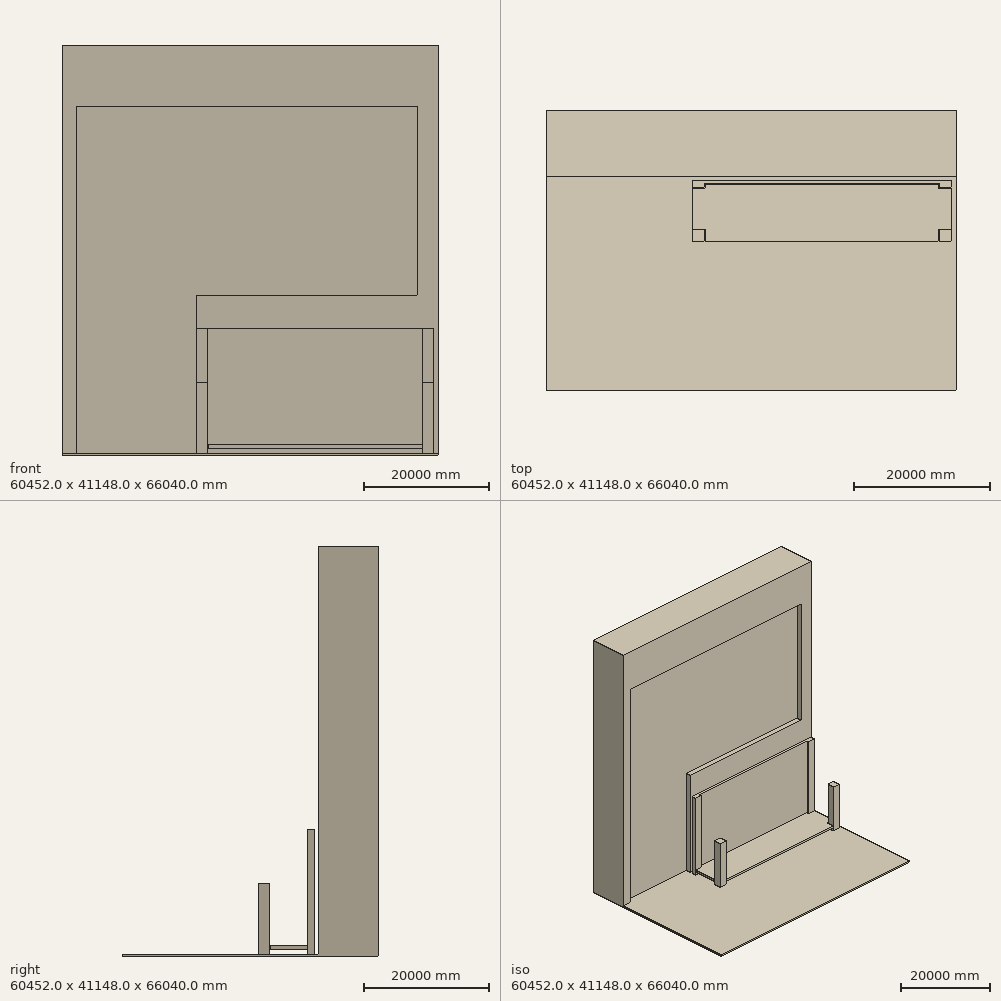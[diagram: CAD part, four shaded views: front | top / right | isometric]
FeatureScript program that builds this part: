
annotation { "Feature Type Name" : "Feature", "Feature Type Description" : "" }
export const myFeature = defineFeature(function(context is Context, id is Id, definition is map)
    precondition{}
    {
        {
            var Q0;
            Q0=qCreatedBy(makeId("Top.planeOp"),FACE);
            var sketch = newSketch(context, id + "F0", { "sketchPlane" : qUnion([Q0])});
            skLineSegment(sketch, "E0.bottom", {"start": v(-60452, 41148) * mm, "end": v(0, 41148) * mm});
            skLineSegment(sketch, "E0.top", {"start": v(-60452, 0) * mm, "end": v(0, 0) * mm});
            skLineSegment(sketch, "E0.left", {"start": v(-60452, 41148) * mm, "end": v(-60452, 0) * mm});
            skLineSegment(sketch, "E0.right", {"start": v(0, 41148) * mm, "end": v(0, 0) * mm});
            skSolve(sketch);
        }
        {
            var Q0;
            Q0=makeQuery(id+"F0.imprint","IMPRINT",FACE,{"disambiguationData":[TD([[makeQuery(id+"F0.imprint","IMPRINT",EDGE,{"derivedFrom":sQuery(id+"F0.wireOp",EDGE,"E0.bottom")}),-1.0]])]});
            extrude(context, id + "F1", {"entities" : qUnion([Q0]), "depth" : 381 * mm, "offsetDistance" : 25.4 * mm});
        }
        {
            var Q0;
            Q0=qCreatedBy(makeId("Top.planeOp"),FACE);
            var sketch = newSketch(context, id + "F2", { "sketchPlane" : qUnion([Q0])});
            skLineSegment(sketch, "E1.bottom", {"start": v(0, 41148) * mm, "end": v(-60452, 41148) * mm});
            skLineSegment(sketch, "E1.top", {"start": v(0, 31496) * mm, "end": v(-60452, 31496) * mm});
            skLineSegment(sketch, "E1.left", {"start": v(0, 41148) * mm, "end": v(0, 31496) * mm});
            skLineSegment(sketch, "E2.right", {"start": v(-60452, 41148) * mm, "end": v(-60452, 31496) * mm});
            skSolve(sketch);
        }
        {
            var Q0;
            Q0 = qSketchRegion(id + "F2", true);
            extrude(context, id + "F3", {"entities" : qUnion([Q0]), "operationType" : NewBodyOperationType.ADD, "depth" : 66040 * mm, "offsetDistance" : 25.4 * mm});
        }
        {
            var Q0;
            Q0=qCreatedBy(makeId("Front.planeOp"),FACE);
            var sketch = newSketch(context, id + "F4", { "sketchPlane" : qUnion([Q0])});
            skLineSegment(sketch, "E3.top", {"start": v(-58293, 381) * mm, "end": v(-38862, 381) * mm});
            skLineSegment(sketch, "E3.left", {"start": v(-58293, 56261) * mm, "end": v(-58293, 381) * mm});
            skLineSegment(sketch, "E3.right", {"start": v(-38862, 25781) * mm, "end": v(-38862, 381) * mm});
            skLineSegment(sketch, "E4.bottom", {"start": v(-38862, 25781) * mm, "end": v(-3302, 25781) * mm});
            skLineSegment(sketch, "E4.right", {"start": v(-3302, 25781) * mm, "end": v(-3302, 56261) * mm});
            skLineSegment(sketch, "E5", {"start": v(-58293, 56261) * mm, "end": v(-3302, 56261) * mm});
            skSolve(sketch);
        }
        {
            var Q0;
            Q0=makeQuery(id+"F4.imprint","IMPRINT",FACE,{"disambiguationData":[TD([[makeQuery(id+"F4.imprint","IMPRINT",EDGE,{"derivedFrom":sQuery(id+"F4.wireOp",EDGE,"E3.top")}),1.0]])]});
            var Q1;
            Q1=sQuery(id+"F0.wireOp",EDGE,"E0.left");
            sweep(context, id + "F5", {"operationType" : NewBodyOperationType.REMOVE, "profiles" : qUnion([Q0]), "path" : qUnion([Q1])});
        }
        {
            var Q0;
            Q0 = qSketchRegion(id + "F4", true);
            extrude(context, id + "F6", {"entities" : qUnion([Q0]), "oppositeDirection" : true, "depth" : 2540 * mm, "offsetDistance" : 25.4 * mm});
        }
        {
            var Q0;
            Q0=makeQuery(id+"F6.opExtrude","SWEPT_BODY",BODY,{"disambiguationData":[OSD([sQuery(id+"F4.wireOp",EDGE,"E3.top"),sQuery(id+"F4.wireOp",EDGE,"E3.left"),sQuery(id+"F4.wireOp",EDGE,"E3.right"),sQuery(id+"F4.wireOp",EDGE,"E4.bottom"),sQuery(id+"F4.wireOp",EDGE,"E4.right"),sQuery(id+"F4.wireOp",EDGE,"E5")])]});
            var Q1;
            Q1=qCreatedBy(makeId("Front.planeOp"),FACE);
            transform(context, id + "F7", {"entities" : qUnion([Q0]), "transformType" : TransformType.TRANSLATION_DISTANCE, "transformDirection" : qUnion([Q1]), "distance" : 32766 * mm, "oppositeDirection" : true, "makeCopy" : false});
        }
        {
            var Q0;
            Q0=qCreatedBy(makeId("Top.planeOp"),FACE);
            cPlane(context, id + "F8", {"entities" : qUnion([Q0]), "cplaneType" : CPlaneType.OFFSET, "offset" : 27432 * mm, "width" : 152.4 * mm, "height" : 152.4 * mm});
        }
        {
            var Q0;
            {var subQ0=sQuery(id+"F0.wireOp",EDGE,"E0.left");Q0=makeQuery(id+"F5.boolean.opBoolean","MERGE",FACE,{"derivedFrom":[makeQuery(id+"F1.opExtrude","CAP_FACE",FACE,{"disambiguationData":[OSD([sQuery(id+"F0.wireOp",EDGE,"E0.bottom"),sQuery(id+"F0.wireOp",EDGE,"E0.top"),subQ0,sQuery(id+"F0.wireOp",EDGE,"E0.right")])],"isStart":false}),makeQuery(id+"F5.opSweep","SWEPT_FACE",FACE,{"disambiguationData":[OSD([subQ0,sQuery(id+"F4.wireOp",EDGE,"E3.top")])]})]});}
            var sketch = newSketch(context, id + "F9", { "sketchPlane" : qUnion([Q0])});
            skLineSegment(sketch, "E6.bottom", {"start": v(-38862, 30937.2) * mm, "end": v(-37084, 30937.2) * mm});
            skLineSegment(sketch, "E6.top", {"start": v(-38862, 21894.8) * mm, "end": v(-37084, 21894.8) * mm});
            skLineSegment(sketch, "E6.left", {"start": v(-38862, 30937.2) * mm, "end": v(-38862, 29794.2) * mm});
            skLineSegment(sketch, "E6.right", {"start": v(-762, 30937.2) * mm, "end": v(-762, 29794.2) * mm});
            skLineSegment(sketch, "E7.bottom", {"start": v(-38862, 23672.8) * mm, "end": v(-37084, 23672.8) * mm});
            skLineSegment(sketch, "E7.right", {"start": v(-37084, 23672.8) * mm, "end": v(-37084, 21894.8) * mm});
            skLineSegment(sketch, "E8.top", {"start": v(-37084, 29794.2) * mm, "end": v(-38862, 29794.2) * mm});
            skLineSegment(sketch, "E8.left", {"start": v(-37084, 30937.2) * mm, "end": v(-37084, 29794.2) * mm});
            skLineSegment(sketch, "E9.bottom", {"start": v(-762, 23672.8) * mm, "end": v(-2540, 23672.8) * mm});
            skLineSegment(sketch, "E9.left", {"start": v(-762, 23672.8) * mm, "end": v(-762, 21894.8) * mm});
            skLineSegment(sketch, "E9.right", {"start": v(-2540, 23672.8) * mm, "end": v(-2540, 21894.8) * mm});
            skLineSegment(sketch, "E10.bottom", {"start": v(-762, 29794.2) * mm, "end": v(-2540, 29794.2) * mm});
            skLineSegment(sketch, "E10.right", {"start": v(-2540, 29794.2) * mm, "end": v(-2540, 30937.2) * mm});
            skLineSegment(sketch, "E11.trimOffspring", {"start": v(-2540, 21894.8) * mm, "end": v(-762, 21894.8) * mm});
            skLineSegment(sketch, "E12.trimOffspring", {"start": v(-38862, 23672.8) * mm, "end": v(-38862, 21894.8) * mm});
            skLineSegment(sketch, "E13.trimOffspring", {"start": v(-2540, 30937.2) * mm, "end": v(-762, 30937.2) * mm});
            skPoint(sketch, "E10.top.end.orphan", {"position": v(-2540, 36383.31) * mm});
            skSolve(sketch);
        }
        {
            var Q0;
            Q0 = qSketchRegion(id + "F9", true);
            extrude(context, id + "F10", {"entities" : qUnion([Q0]), "operationType" : NewBodyOperationType.ADD, "depth" : 11430 * mm, "offsetDistance" : 25.4 * mm});
        }
        {
            var Q0;
            Q0=makeQuery(id+"F10.opExtrude","CAP_FACE",FACE,{"disambiguationData":[OSD([sQuery(id+"F9.wireOp",EDGE,"E6.bottom"),sQuery(id+"F9.wireOp",EDGE,"E6.left"),sQuery(id+"F9.wireOp",EDGE,"E8.top"),sQuery(id+"F9.wireOp",EDGE,"E8.left")])],"isStart":false});
            extrude(context, id + "F11", {"entities" : qUnion([Q0]), "operationType" : NewBodyOperationType.ADD, "depth" : 8636 * mm, "offsetDistance" : 25.4 * mm});
        }
        {
            var Q0;
            Q0=makeQuery(id+"F10.opExtrude","CAP_FACE",FACE,{"disambiguationData":[OSD([sQuery(id+"F9.wireOp",EDGE,"E6.right"),sQuery(id+"F9.wireOp",EDGE,"E10.bottom"),sQuery(id+"F9.wireOp",EDGE,"E10.right"),sQuery(id+"F9.wireOp",EDGE,"E13.trimOffspring")])],"isStart":false});
            extrude(context, id + "F12", {"entities" : qUnion([Q0]), "operationType" : NewBodyOperationType.ADD, "depth" : 8636 * mm, "offsetDistance" : 25.4 * mm});
        }
        {
            var Q0;
            {var subQ0=sQuery(id+"F9.wireOp",EDGE,"E13.trimOffspring");Q0=makeQuery(id+"F12.boolean.opBoolean","MERGE",FACE,{"derivedFrom":[makeQuery(id+"F10.opExtrude","SWEPT_FACE",FACE,{"disambiguationData":[OSD([subQ0])]}),makeQuery(id+"F12.opExtrude","SWEPT_FACE",FACE,{"disambiguationData":[OSD([subQ0])]})]});}
            var sketch = newSketch(context, id + "F13", { "sketchPlane" : qUnion([Q0])});
            skLineSegment(sketch, "E14.bottom", {"start": v(38862, 20447) * mm, "end": v(762, 20447) * mm});
            skLineSegment(sketch, "E14.top", {"start": v(38862, 1143) * mm, "end": v(762, 1143) * mm});
            skLineSegment(sketch, "E14.left", {"start": v(38862, 20447) * mm, "end": v(38862, 1143) * mm});
            skLineSegment(sketch, "E14.right", {"start": v(762, 20447) * mm, "end": v(762, 1143) * mm});
            skSolve(sketch);
        }
        {
            var Q0;
            {var subQ5=sQuery(id+"F13.wireOp",EDGE,"E14.left");Q0=makeQuery(id+"F13.imprint","IMPRINT",FACE,{"disambiguationData":[TD([[makeQuery(id+"F13.imprint","IMPRINT",EDGE,{"derivedFrom":subQ5}),-1.0]])]});}
            extrude(context, id + "F14", {"entities" : qUnion([Q0]), "operationType" : NewBodyOperationType.ADD, "oppositeDirection" : true, "depth" : 546.1 * mm, "offsetDistance" : 25.4 * mm, "hasSecondDirection" : true, "secondDirectionOppositeDirection" : true, "secondDirectionDepth" : -25.4 * mm});
        }
        {
            var Q0;
            Q0=makeQuery(id+"F14.opExtrude","SWEPT_FACE",FACE,{"disambiguationData":[OSD([sQuery(id+"F13.wireOp",EDGE,"E14.top")])]});
            var sketch = newSketch(context, id + "F15", { "sketchPlane" : qUnion([Q0])});
            skLineSegment(sketch, "E15.bottom", {"start": v(-2590.8, -30365.7) * mm, "end": v(-37033.2, -30365.7) * mm});
            skLineSegment(sketch, "E15.top", {"start": v(-2590.8, -21894.8) * mm, "end": v(-37033.2, -21894.8) * mm});
            skLineSegment(sketch, "E15.left", {"start": v(-38862, -29743.4) * mm, "end": v(-38862, -23723.6) * mm});
            skLineSegment(sketch, "E15.right", {"start": v(-762, -29743.4) * mm, "end": v(-762, -23723.6) * mm});
            skLineSegment(sketch, "E16.bottom", {"start": v(-38862, -23723.6) * mm, "end": v(-37033.2, -23723.6) * mm});
            skLineSegment(sketch, "E16.right", {"start": v(-37033.2, -23723.6) * mm, "end": v(-37033.2, -21894.8) * mm});
            skLineSegment(sketch, "E17.bottom", {"start": v(-2590.8, -23723.6) * mm, "end": v(-762, -23723.6) * mm});
            skLineSegment(sketch, "E17.left", {"start": v(-2590.8, -23723.6) * mm, "end": v(-2590.8, -21894.8) * mm});
            skLineSegment(sketch, "E18.top", {"start": v(-37033.2, -29743.4) * mm, "end": v(-38862, -29743.4) * mm});
            skLineSegment(sketch, "E18.left", {"start": v(-37033.2, -30365.7) * mm, "end": v(-37033.2, -29743.4) * mm});
            skLineSegment(sketch, "E19.bottom", {"start": v(-762, -29743.4) * mm, "end": v(-2590.8, -29743.4) * mm});
            skLineSegment(sketch, "E19.right", {"start": v(-2590.8, -29743.4) * mm, "end": v(-2590.8, -30365.7) * mm});
            skSolve(sketch);
        }
        {
            var Q0;
            Q0=makeQuery(id+"F15.imprint","IMPRINT",FACE,{"disambiguationData":[TD([[makeQuery(id+"F15.imprint","IMPRINT",EDGE,{"derivedFrom":sQuery(id+"F15.wireOp",EDGE,"E15.bottom")}),-1.0]])]});
            extrude(context, id + "F16", {"entities" : qUnion([Q0]), "oppositeDirection" : true, "depth" : 558.8 * mm, "offsetDistance" : 25.4 * mm});
        }
    });
